# Revit family: Varmax 180-225_4 tomas
name_source: partatom
category: Mechanical Equipment
revit_build: Autodesk Revit 2014 (Build: 20130308_1515(x64)
units: mm (PartAtom-declared; Revit-internal decimal feet)

## types (2) — shared parameters
Alt. conec. = 1564 mm
Alt. derivación gas = 1315 mm  [stored 4.3143 ft]
Alt. entrada de aire = 1606 mm  [stored 5.26903 ft]
Alt. entrada/salida retorno = 1171 mm  [stored 3.84186 ft]
Altura = 1780 mm
Ancho = 734 mm  [stored 2.40814 ft]
Assembly Code = D3020100
Conector = 169 mm  [stored 0.554462 ft]
Configuración = 4 tomas
Derivacion gas = 38 mm
Derivación de vaciado = 25 mm  [stored 0.082021 ft]
Derivación salida / retorno = 51 mm
Empresa creadora del BIM = ACAE
Entrada de aire = 150 mm
Manufacturer = Atlantic
Mínimo = 45 mm
Peso en vacío = 450 kg
Presión máxima de servicio = 6 bar
Rendimiento mínimo al 100% de potencia (80/60 ºC) = 97,6%
Rendimiento mínimo al 30% de carga (50/30 ºC) = 109,1%
Salida de humo = 150 mm
Salida de humos = 150 mm
Tipo de combustible = Gas natural (G20), en opción Gas propano (G31) hasta 320 kW.
URL = http://www.ygnis.es
Volumen de agua = 151 L

## per-type parameters (varying)
| type | Caudal de gas a Pn (15 °C) | Consumo eléctrico máximo | Description | Model | Potencia útil (50/30 ºC) | Profundidad Total |
| Varmax 180 - Caldera de pie de condensación a gas 191 kW y 6 bar (4 tomas) | 19,05 m3/h | 179 W | Unidad térmica de condensación para gas natural Ygnis modelo Varmax 180,  potencia útil (50/30 ºC) de 191 kW. Fabricada en acero inoxidable de alta calidad AISI 316 L. Quemador modulante desde el 20% de la potencia. Rendimiento hasta el 107 %. Clase 5 de NOx. Dimensiones (Altura x Ancho x Largo): 1834 x 700 x 1193 mm. Peso en vacío: 450 kg. Presión máxima de servicio: 6 bar. Configuración a 4 tomas.
en acero inoxidable con potencias comprendidas entre
127 y 478kW. | Varmax 180 | 191 kW | 1218 mm  [stored 3.99606 ft] |
| Varmax 225 - Caldera de pie de condensación a gas 238 kW y 6 bar (4 tomas) | 23,81 m3/h | 320 W | Unidad térmica de condensación para gas natural Ygnis modelo Varmax 225,  potencia útil (50/30 ºC) de 238 kW. Fabricada en acero inoxidable de alta calidad AISI 316 L. Quemador modulante desde el 20% de la potencia. Rendimiento hasta el 107 %. Clase 5 de NOx. Dimensiones (Altura x Ancho x Largo): 1834 x 700 x 1193 mm. Peso en vacío: 450 kg. Presión máxima de servicio: 6 bar. Configuración a 4 tomas. | Varmax Varmax 225 | 238 kW | 1241 mm |

note: [stored X ft] marks values corroborated as IEEE doubles in the binary element streams (Revit-internal decimal feet)

## geometry (parser evidence)
native form markers: Sweep x1
no freeform markers — native parametric forms only
